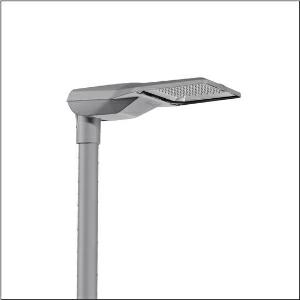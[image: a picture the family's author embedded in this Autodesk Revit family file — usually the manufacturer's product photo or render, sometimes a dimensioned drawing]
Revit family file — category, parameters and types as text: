
# Revit family: streetlight_sl_21_iq_midi___st1_0a_5xe3d41g08mb_322d
name_source: partatom
category: Lighting Fixtures
units: mm (PartAtom-declared; Revit-internal decimal feet)

## family parameters
Cut with Voids When Loaded = No
Host = Face
Light Source = No
Part Type = Normal
Room Calculation Point = No
Round Connector Dimension = Use Diameter
Shared = No

## types (1)
- --- (1 x LED, 20360 lm, 146.7 W, 4000K)
    Apparent Load = 147 VA
    CIE Flux Codes = 37 72 97 100 100
    Color Rendering = 70
    Color Temperature = 4000K
    Default Elevation = 1800 mm
    Description = Streetlight SL 21 iQ midi, mast luminaire, primary light control with lens, of PMMA, primary optical cover: cover, of toughened safety glass, transparent, light distribution: ST1.0a, light emission: direct distribution, primary light characteristic: asymmetric, installation type: post-top, side-entry, LED, High Power LED, rated luminous flux: 20.360lm, luminous efficacy: 139lm/W, light colour: 740, colour temperature: 4000K, control: Street-Remote, Auto-Match, Temp-Guard, Lumen-Switch, Night-Set, Smart-Wire, Light-Fading, Desk-Remote (wireless, voltage-free reading and setting of iQ features in the workshop via application-optimized NFC function/RFID function), optimised constant luminous flux control (CLO 2.0), presetting dimming linear, mains connection: 230..240V, AC, 50/60Hz, start of lifetime: 147W, end of service life: 161W, reduction: 62W, luminaire housing, of diecast aluminium, powder-coated, Siteco® metallic grey (DB 702S), corrosivity category C5 mid according to DIN EN ISO 12944, please order mast flange separately, inclination adjustable: 0°, 5°, 10°, 15°, sealing non-destructively replaceable, multi-level sealing system, length: 644mm, width: 335mm, height: 110mm, mast flange for spigot size: 42mm (side-entry): 5XC10008XM4, 60/48mm (side-entry/post-top): 5XC10108XM2, 76/60mm (side-entry/post-top): 5XC10108XM1, protection rating (complete): IP66, insulation class (complete): insulation class II (safety insulation), certification: CE, ENEC, ENEC+, VDE, impact resistance: IK09, permissible operating ambient temperature for outdoor applications: -40..+50°C, standard-compliant lighting for roads and squares, packaging unit: 1 piece

Light Distribution: ST1.0a
    Height = 111 mm
    Lamp = 1 x LED
    Lamp Light Flux = 20360 lm
    Lamp Power = 146.7 W
    Lamp count = 1
    Length = 644 mm
    Luminous efficacy = 139 lm/W
    Manufacturer = Siteco
    ModVariant = No
    Model = 5XE3D41G08MB
    Number of Poles = 1
    OnlyDefault = Yes
    Power Factor = 1
    Product Name = Streetlight SL 21 iQ midi | ST1.0a
    Product group = mast luminaire | pylon top
    ProductGroupID = 6100
    Protection Class = Protection class II
    Protection Degree = IP 66
    RLX_Detail_Level = 1
    RLX_Emergency_Light_Flux = 0 lm
    RLX_Emergency_Type = 0
    RLX_Emergency_Type_DB = No
    RlxData = <blob elided: 91413 chars, md5=0ee114e8>
    Socket = socket
    Standby Power = 0 W
    System Light Flux = 20360 lm
    System Power = 147 W
    Type Comments = factory setting: luminous flux: 100 % | dim-lin: 254 | 753 mA
    Type Image = l_1004298.jpg
    URL = http://relux.com
    VarID = @adj_123411
    Voltage = 0 V
    Weight = 0.00 kg
    Width = 336 mm

## geometry (parser evidence)
native form markers: Blend x4, Sweep x10
no freeform markers — native parametric forms only
